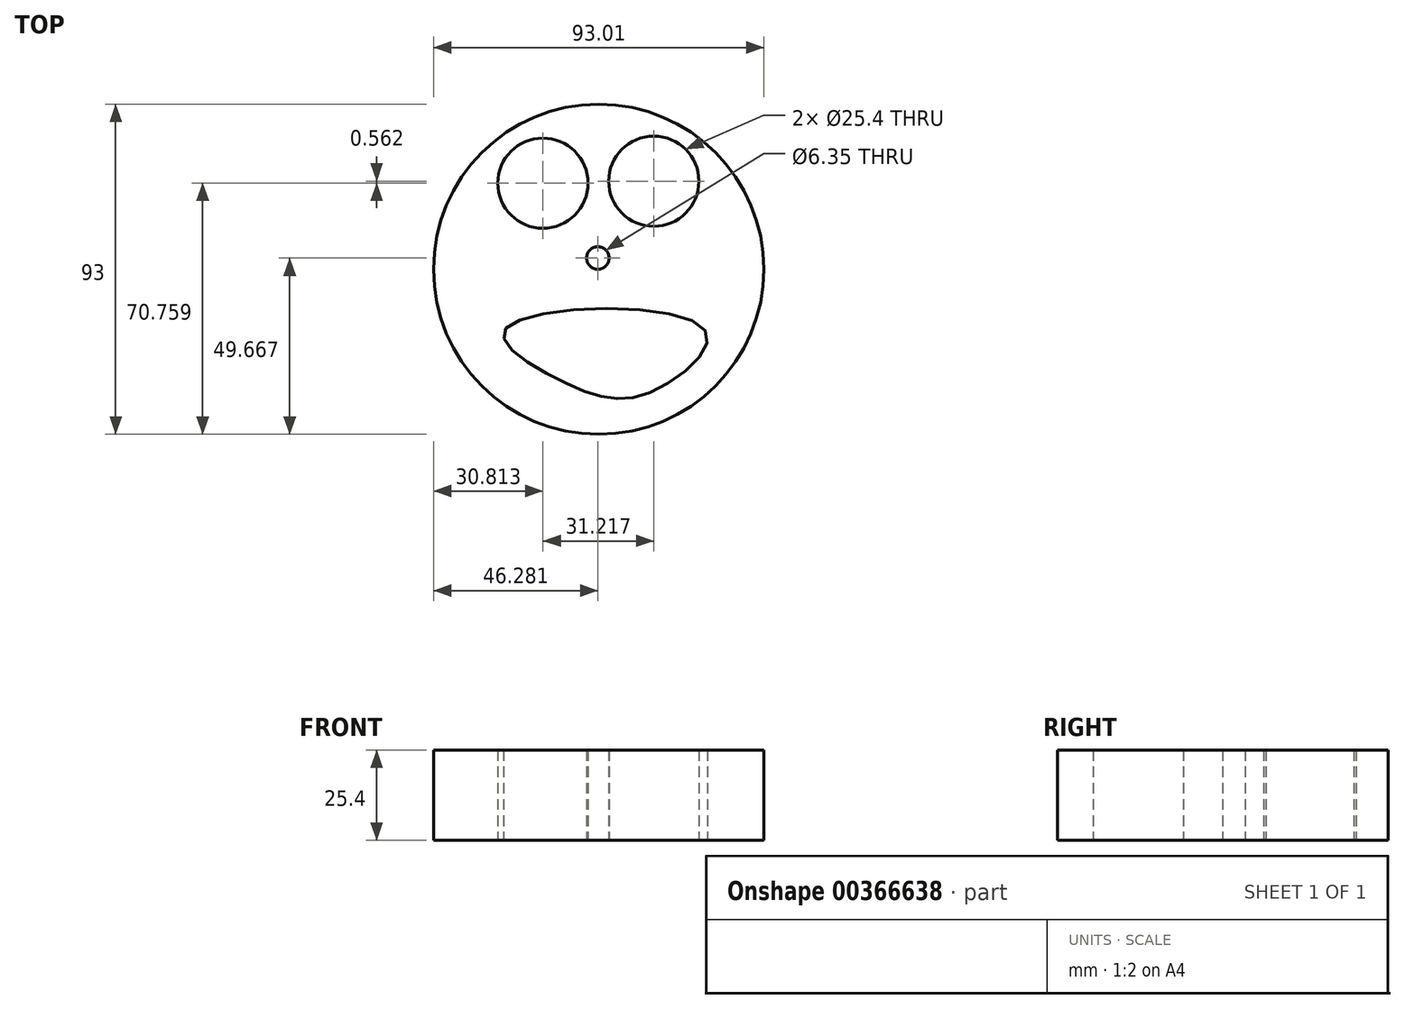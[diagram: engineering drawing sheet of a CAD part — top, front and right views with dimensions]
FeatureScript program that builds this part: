
annotation { "Feature Type Name" : "Feature", "Feature Type Description" : "" }
export const myFeature = defineFeature(function(context is Context, id is Id, definition is map)
    precondition{}
    {
        {
            var Q0;
            Q0=qCreatedBy(makeId("Top.planeOp"),FACE);
            var sketch = newSketch(context, id + "F0", { "sketchPlane" : qUnion([Q0])});
            skCircle(sketch, "E0", {"center": v(-15.52, 16.66) * mm, "radius": 46.5 * mm});
            skCircle(sketch, "E1", {"center": v(-31.22, 40.92) * mm, "radius": 12.7 * mm});
            skCircle(sketch, "E2", {"center": v(0, 41.48) * mm, "radius": 12.7 * mm});
            skCircle(sketch, "E3", {"center": v(-15.75, 19.83) * mm, "radius": 3.18 * mm});
            skFitSpline(sketch, "E4", {"points": [v(-41.62, 0) * mm, v(-24.47, -15.6) * mm, v(0, -17.58) * mm, v(14.06, 0) * mm, v(-41.62, 0) * mm]});
            skSolve(sketch);
        }
        {
            var Q0;
            Q0=makeQuery(id+"F0.imprint","IMPRINT",FACE,{"disambiguationData":[TD([[makeQuery(id+"F0.imprint","IMPRINT",EDGE,{"derivedFrom":sQuery(id+"F0.wireOp",EDGE,"E0")}),1.0]])]});
            extrude(context, id + "F1", {"entities" : qUnion([Q0]), "depth" : 25.4 * mm});
        }
    });
